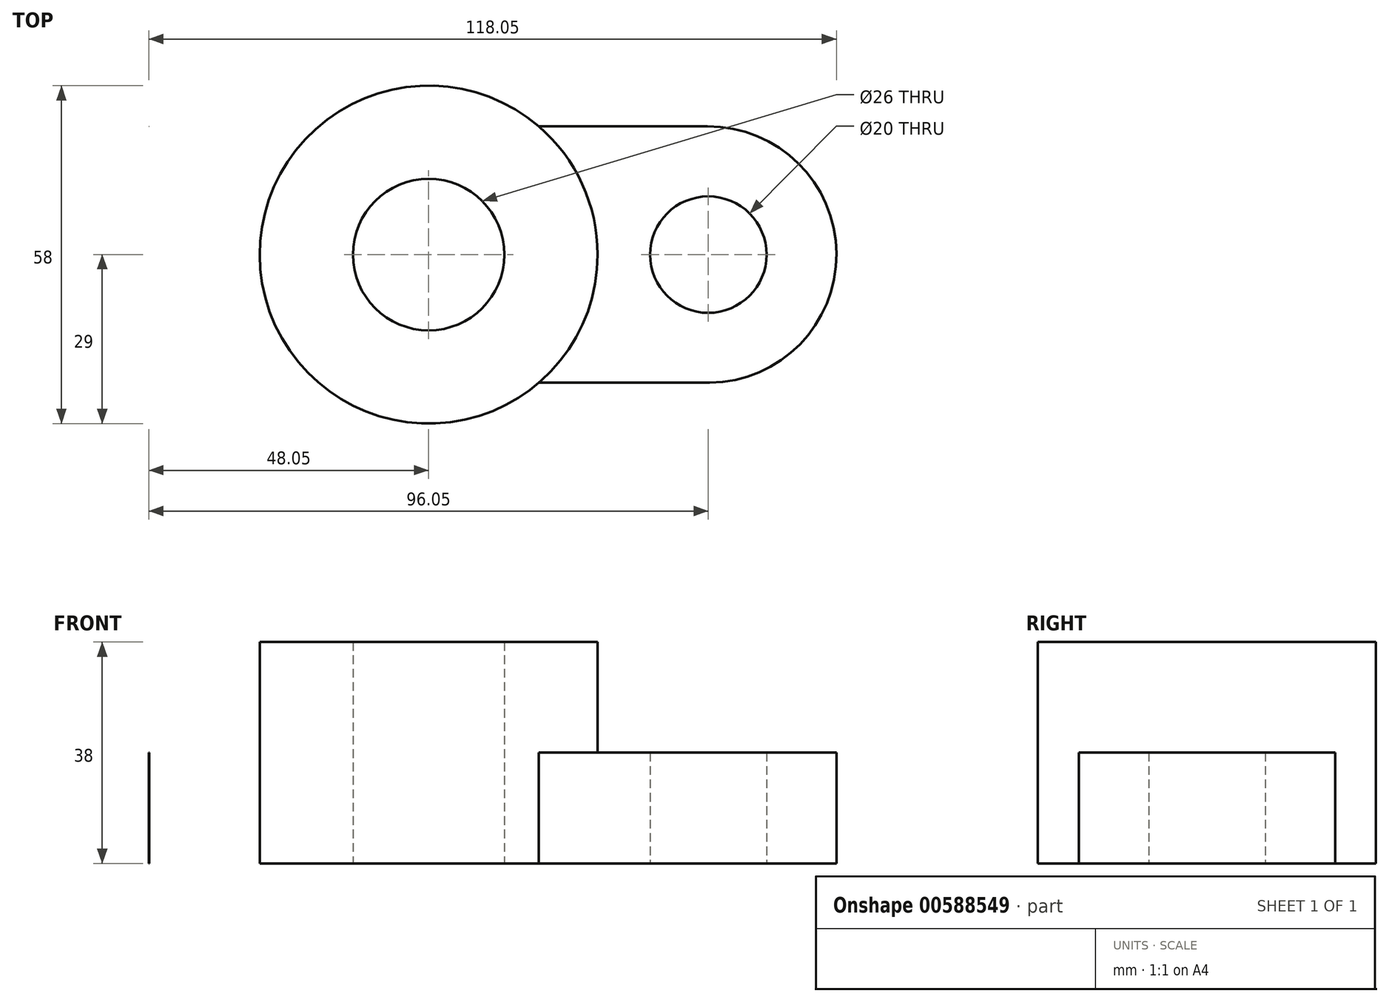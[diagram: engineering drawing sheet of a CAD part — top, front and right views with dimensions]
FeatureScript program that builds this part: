
annotation { "Feature Type Name" : "Feature", "Feature Type Description" : "" }
export const myFeature = defineFeature(function(context is Context, id is Id, definition is map)
    precondition{}
    {
        {
            var Q0;
            Q0=qCreatedBy(makeId("Top.planeOp"),FACE);
            var sketch = newSketch(context, id + "F0", { "sketchPlane" : qUnion([Q0])});
            skCircle(sketch, "E0", {"center": v(0, 0) * mm, "radius": 29 * mm});
            skArc(sketch, "E1", {"start": v(-47.95, 22) * mm, "mid": v(-70, 0.01) * mm, "end": v(-47.97, -22) * mm});
            skArc(sketch, "E2", {"start": v(47.8, -22) * mm, "mid": v(70, -0.02) * mm, "end": v(47.82, 22) * mm});
            skCircle(sketch, "E3", {"center": v(-48, 0) * mm, "radius": 10 * mm});
            skCircle(sketch, "E4", {"center": v(48, 0) * mm, "radius": 10 * mm});
            skLineSegment(sketch, "E5", {"start": v(-48.03, -22) * mm, "end": v(-18.9, -22) * mm});
            skLineSegment(sketch, "E6", {"start": v(48.2, -22) * mm, "end": v(18.9, -22) * mm});
            skLineSegment(sketch, "E7", {"start": v(47.82, 22) * mm, "end": v(18.9, 22) * mm});
            skLineSegment(sketch, "E8", {"start": v(-48.05, 22) * mm, "end": v(-18.9, 22) * mm});
            skCircle(sketch, "E9", {"center": v(0, 0) * mm, "radius": 13 * mm});
            skSolve(sketch);
        }
        {
            var Q0;
            Q0=makeQuery(id+"F0.imprint","IMPRINT",FACE,{"disambiguationData":[TD([[makeQuery(id+"F0.imprint","IMPRINT",EDGE,{"derivedFrom":sQuery(id+"F0.wireOp",EDGE,"E9")}),-1.0]])]});
            extrude(context, id + "F1", {"entities" : qUnion([Q0]), "depth" : 38 * mm, "offsetDistance" : 25 * mm});
        }
        {
            var Q0;
            Q0=makeQuery(id+"F0.imprint","IMPRINT",FACE,{"disambiguationData":[TD([[makeQuery(id+"F0.imprint","IMPRINT",EDGE,{"derivedFrom":sQuery(id+"F0.wireOp",EDGE,"E4")}),-1.0]])]});
            var Q1;
            {var subQ1=sQuery(id+"F0.wireOp",EDGE,"E1");Q1=makeQuery(id+"F0.imprint","IMPRINT",FACE,{"disambiguationData":[TD([[makeQuery(id+"F0.imprint","IMPRINT",EDGE,{"derivedFrom":subQ1}),1.0]])]});}
            extrude(context, id + "F2", {"entities" : qUnion([Q0, Q1]), "operationType" : NewBodyOperationType.ADD, "depth" : 19 * mm, "offsetDistance" : 25 * mm});
        }
    });
